# Revit family: Storage_Tank-Rheem--
name_source: partatom
category: Mechanical Equipment
units: mm (PartAtom-declared; Revit-internal decimal feet)

## family parameters
Always vertical = Yes
Classification = None
Cut with Voids When Loaded = No
OmniClass Number = 23.65.00.00
OmniClass Title = Supply and Distribution of Liquids and Gases
Part Type = Normal
Room Calculation Point = No
Round Connector Dimension = Use Diameter
Shared = No
Work Plane-Based = No

## types (3) — shared parameters
Assembly Code = D3020
Description = Air Sourced Heat Pump Water Heater
ENGworks Global = www.ENGworksGlobal.com
Manufacturer = Rheem
Maximum Power Input = 147 kW
Maximum Stored Water Temperature = 85 °C
Maximum Water Supply Pressure = 560.00 kPa
Product Page URL = https://www.rheem.com.au
Tank Material = Metal - Rheem - Stainless Steel
Top Hook Height = 110 mm  [stored 0.360892 ft]
URL = https://www.rheem.com.au
Version = 1
zero-valued in all types: Default Elevation

## per-type parameters (varying)
| type | Base Mount Offset From Center | Cold Water Inlet Offset | Hot Water Flow Return Offset | Hot Water Supply Offset | Storage Capacity | Tank Height | Tank Outside Diameter | Tank Outside Radius | Weight Empty |
| 1000L | 220 mm | 417 mm | 879 mm | 1803 mm | 3000 L | 2200 mm | 880 mm  [stored 2.88714 ft] | 440  [stored 1.44357 ft] | 400.00 kgf |
| 2000L | 325 mm | 462 mm | 1024 mm | 1700 mm | 2000 L | 2090 mm | 1300 mm | 650 | 330.00 kgf |
| 3000L | 325 mm | 505 mm | 1135 mm | 2395 mm | 3000 L | 2990 mm | 1300 mm | 650 | 400.00 kgf |

note: column(s) folded — value = type name in every type: Model

note: [stored X ft] marks values corroborated as IEEE doubles in the binary element streams (Revit-internal decimal feet)

## geometry (parser evidence)
native form markers: Blend x4, Sweep x4
no freeform markers — native parametric forms only
